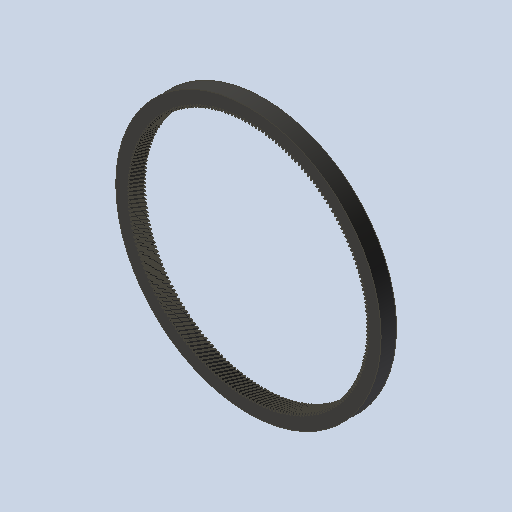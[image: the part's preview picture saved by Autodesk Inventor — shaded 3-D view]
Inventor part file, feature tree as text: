
AUTODESK INVENTOR PART (.ipt)
format: ipt  version: 2023 (Build 270158000, 158)  size: 2,475,008 bytes
history: native  units: mm (DEFAULTED — no unit token found)
features: plane x3, other x3, sketch x2, extrude x1
ambient origin geometry x8: Origin, YZ Plane, XZ Plane, XY Plane, X Axis, Y Axis, Z Axis, Center Point
bodies: Solid1 (feature_tree)
feature tree (9):
  extrude  "Extrusion1"  Depth=15.0mm TaperAngle=0.0deg
  plane  "Work Plane2"
  plane  "Work Plane8"
  plane  "Work Plane9"
  other  "Spur Gear"
  sketch  "Sketch1"  dims[d0=257.87614mm d1=15.0mm d2=0.0mm]
  sketch  "Sketch2"  dims[d3=231.990754mm d4=10.0mm d5=0.0mm d16=101.6mm d17=0.0mm d34=0.14411mm d39=0.0mm d45=0.0mm d47=101.6mm d50=0.0mm d51=0.0mm d52=101.6mm]
  other  "Srf1"
  other  "Pitch Diameter"
